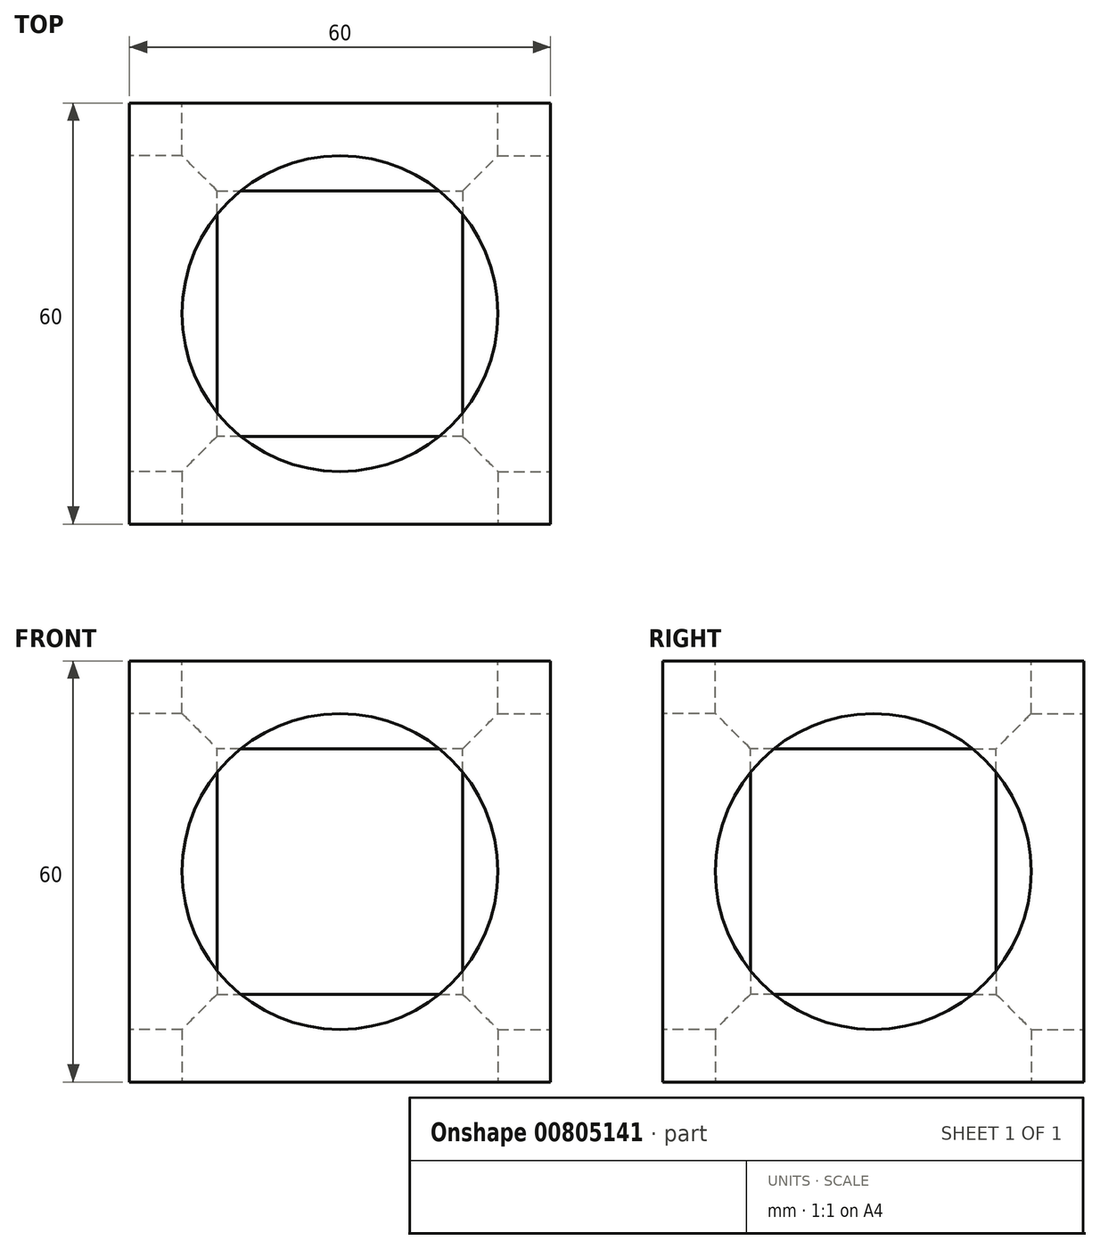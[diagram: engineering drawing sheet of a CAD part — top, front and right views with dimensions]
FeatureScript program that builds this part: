
annotation { "Feature Type Name" : "Feature", "Feature Type Description" : "" }
export const myFeature = defineFeature(function(context is Context, id is Id, definition is map)
    precondition{}
    {
        {
            assignVariable(context, id + "F0", {"name" : "L", "anyValue" : 60 * mm});
        }
        {
            assignVariable(context, id + "F1", {"name" : "P", "anyValue" : 12.5 * mm});
        }
        {
            var Q0;
            Q0=qCreatedBy(makeId("Top.planeOp"),FACE);
            var sketch = newSketch(context, id + "F2", { "sketchPlane" : qUnion([Q0])});
            skLineSegment(sketch, "E0.bottom", {"start": v(-30, 30) * mm, "end": v(30, 30) * mm});
            skLineSegment(sketch, "E0.top", {"start": v(-30, -30) * mm, "end": v(30, -30) * mm});
            skLineSegment(sketch, "E0.left", {"start": v(-30, 30) * mm, "end": v(-30, -30) * mm});
            skLineSegment(sketch, "E0.right", {"start": v(30, 30) * mm, "end": v(30, -30) * mm});
            skSolve(sketch);
        }
        {
            var Q0;
            Q0 = qSketchRegion(id + "F2", true);
            extrude(context, id + "F3", {"entities" : qUnion([Q0]), "depth" : getVariable(context, 'L') / 2, "offsetDistance" : 25 * mm, "hasSecondDirection" : true, "secondDirectionOppositeDirection" : true, "secondDirectionDepth" : getVariable(context, 'L') / 2});
        }
        {
            var Q0;
            Q0=makeQuery(id+"F3.opExtrude","CAP_FACE",FACE,{"disambiguationData":[OSD([sQuery(id+"F2.wireOp",EDGE,"E0.bottom"),sQuery(id+"F2.wireOp",EDGE,"E0.top"),sQuery(id+"F2.wireOp",EDGE,"E0.left"),sQuery(id+"F2.wireOp",EDGE,"E0.right")])],"isStart":false});
            var sketch = newSketch(context, id + "F4", { "sketchPlane" : qUnion([Q0])});
            skPoint(sketch, "E1", {"position": v(0, 0) * mm});
            skCircle(sketch, "E2", {"center": v(0, 0) * mm, "radius": 22.5 * mm});
            skSolve(sketch);
        }
        {
            var Q0;
            Q0=makeQuery(id+"F3.opExtrude","SWEPT_FACE",FACE,{"disambiguationData":[OSD([sQuery(id+"F2.wireOp",EDGE,"E0.top")])]});
            var sketch = newSketch(context, id + "F5", { "sketchPlane" : qUnion([Q0])});
            skCircle(sketch, "E3", {"center": v(0, 0) * mm, "radius": 22.5 * mm});
            skSolve(sketch);
        }
        {
            var Q0;
            Q0=makeQuery(id+"F3.opExtrude","SWEPT_FACE",FACE,{"disambiguationData":[OSD([sQuery(id+"F2.wireOp",EDGE,"E0.left")])]});
            var sketch = newSketch(context, id + "F6", { "sketchPlane" : qUnion([Q0])});
            skCircle(sketch, "E4", {"center": v(0, 0) * mm, "radius": 22.5 * mm});
            skSolve(sketch);
        }
        {
            var Q0;
            Q0=makeQuery(id+"F3.opExtrude","SWEPT_FACE",FACE,{"disambiguationData":[OSD([sQuery(id+"F2.wireOp",EDGE,"E0.bottom")])]});
            var sketch = newSketch(context, id + "F7", { "sketchPlane" : qUnion([Q0])});
            skCircle(sketch, "E5", {"center": v(0, 0) * mm, "radius": 22.5 * mm});
            skSolve(sketch);
        }
        {
            var Q0;
            Q0=makeQuery(id+"F3.opExtrude","SWEPT_FACE",FACE,{"disambiguationData":[OSD([sQuery(id+"F2.wireOp",EDGE,"E0.right")])]});
            var sketch = newSketch(context, id + "F8", { "sketchPlane" : qUnion([Q0])});
            skCircle(sketch, "E6", {"center": v(0, 0) * mm, "radius": 22.5 * mm});
            skSolve(sketch);
        }
        {
            var Q0;
            Q0=makeQuery(id+"F3.opExtrude","CAP_FACE",FACE,{"disambiguationData":[OSD([sQuery(id+"F2.wireOp",EDGE,"E0.bottom"),sQuery(id+"F2.wireOp",EDGE,"E0.top"),sQuery(id+"F2.wireOp",EDGE,"E0.left"),sQuery(id+"F2.wireOp",EDGE,"E0.right")])],"isStart":true});
            var sketch = newSketch(context, id + "F9", { "sketchPlane" : qUnion([Q0])});
            skCircle(sketch, "E7", {"center": v(0, 0) * mm, "radius": 22.5 * mm});
            skSolve(sketch);
        }
        {
            var Q0;
            Q0=makeQuery(id+"F9.imprint","IMPRINT",FACE,{"disambiguationData":[TD([[makeQuery(id+"F9.imprint","IMPRINT",EDGE,{"derivedFrom":sQuery(id+"F9.wireOp",EDGE,"E7")}),1.0]])]});
            extrude(context, id + "F10", {"entities" : qUnion([Q0]), "operationType" : NewBodyOperationType.REMOVE, "oppositeDirection" : true, "depth" : getVariable(context, 'P'), "offsetDistance" : 25 * mm});
        }
        {
            var Q0;
            Q0=makeQuery(id+"F6.imprint","IMPRINT",FACE,{"disambiguationData":[TD([[makeQuery(id+"F6.imprint","IMPRINT",EDGE,{"derivedFrom":sQuery(id+"F6.wireOp",EDGE,"E4")}),1.0]])]});
            extrude(context, id + "F11", {"entities" : qUnion([Q0]), "operationType" : NewBodyOperationType.REMOVE, "oppositeDirection" : true, "depth" : getVariable(context, 'P'), "offsetDistance" : 25 * mm});
        }
        {
            var Q0;
            Q0=makeQuery(id+"F5.imprint","IMPRINT",FACE,{"disambiguationData":[TD([[makeQuery(id+"F5.imprint","IMPRINT",EDGE,{"derivedFrom":sQuery(id+"F5.wireOp",EDGE,"E3")}),1.0]])]});
            extrude(context, id + "F12", {"entities" : qUnion([Q0]), "operationType" : NewBodyOperationType.REMOVE, "oppositeDirection" : true, "depth" : getVariable(context, 'P'), "offsetDistance" : 25 * mm});
        }
        {
            var Q0;
            Q0=makeQuery(id+"F8.imprint","IMPRINT",FACE,{"disambiguationData":[TD([[makeQuery(id+"F8.imprint","IMPRINT",EDGE,{"derivedFrom":sQuery(id+"F8.wireOp",EDGE,"E6")}),1.0]])]});
            extrude(context, id + "F13", {"entities" : qUnion([Q0]), "operationType" : NewBodyOperationType.REMOVE, "oppositeDirection" : true, "depth" : getVariable(context, 'P'), "offsetDistance" : 25 * mm});
        }
        {
            var Q0;
            Q0=makeQuery(id+"F7.imprint","IMPRINT",FACE,{"disambiguationData":[TD([[makeQuery(id+"F7.imprint","IMPRINT",EDGE,{"derivedFrom":sQuery(id+"F7.wireOp",EDGE,"E5")}),1.0]])]});
            extrude(context, id + "F14", {"entities" : qUnion([Q0]), "operationType" : NewBodyOperationType.REMOVE, "oppositeDirection" : true, "depth" : getVariable(context, 'P'), "offsetDistance" : 25 * mm});
        }
        {
            var Q0;
            Q0=makeQuery(id+"F4.imprint","IMPRINT",FACE,{"disambiguationData":[TD([[makeQuery(id+"F4.imprint","IMPRINT",EDGE,{"derivedFrom":sQuery(id+"F4.wireOp",EDGE,"E2")}),1.0]])]});
            extrude(context, id + "F15", {"entities" : qUnion([Q0]), "operationType" : NewBodyOperationType.REMOVE, "oppositeDirection" : true, "depth" : getVariable(context, 'P'), "offsetDistance" : 25 * mm});
        }
    });
